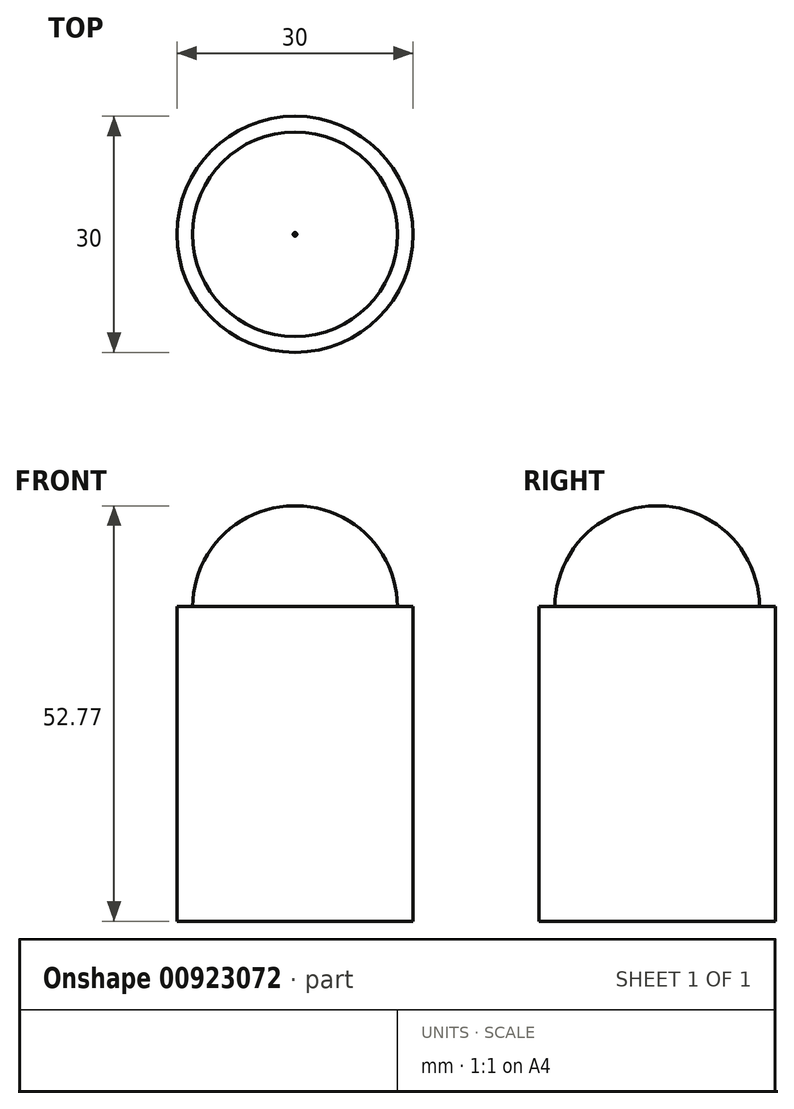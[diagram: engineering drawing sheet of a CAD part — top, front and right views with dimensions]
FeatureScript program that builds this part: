
annotation { "Feature Type Name" : "Feature", "Feature Type Description" : "" }
export const myFeature = defineFeature(function(context is Context, id is Id, definition is map)
    precondition{}
    {
        {
            var Q0;
            Q0=qCreatedBy(makeId("Top.planeOp"),FACE);
            var sketch = newSketch(context, id + "F0", { "sketchPlane" : qUnion([Q0])});
            skCircle(sketch, "E0", {"center": v(0, 0) * mm, "radius": 15 * mm});
            skSolve(sketch);
        }
        {
            var Q0;
            Q0=makeQuery(id+"F0.imprint","IMPRINT",FACE,{"disambiguationData":[TD([[makeQuery(id+"F0.imprint","IMPRINT",EDGE,{"derivedFrom":sQuery(id+"F0.wireOp",EDGE,"E0")}),1.0]])]});
            extrude(context, id + "F1", {"entities" : qUnion([Q0]), "depth" : 25 * mm, "offsetDistance" : 25 * mm});
        }
        {
            var Q0;
            Q0=qCreatedBy(makeId("Front.planeOp"),FACE);
            var sketch = newSketch(context, id + "F2", { "sketchPlane" : qUnion([Q0])});
            skLineSegment(sketch, "E1", {"start": v(-15, 25) * mm, "end": v(0, 25) * mm});
            skLineSegment(sketch, "E2", {"start": v(0, 25) * mm, "end": v(0, 27) * mm});
            skLineSegment(sketch, "E3", {"start": v(0, 27) * mm, "end": v(0, 42) * mm});
            skLineSegment(sketch, "E4", {"start": v(-15, 25) * mm, "end": v(-15, 40) * mm});
            skLineSegment(sketch, "E5", {"start": v(-15, 40) * mm, "end": v(-13, 40) * mm});
            skArc(sketch, "E6", {"start": v(-13, 40) * mm, "mid": v(-9.23, 30.77) * mm, "end": v(0, 27) * mm});
            skSolve(sketch);
        }
        {
            var Q0;
            Q0=makeQuery(id+"F2.imprint","IMPRINT",FACE,{"disambiguationData":[TD([[makeQuery(id+"F2.imprint","IMPRINT",EDGE,{"derivedFrom":sQuery(id+"F2.wireOp",EDGE,"E1")}),1.0]])]});
            var Q1;
            Q1=sQuery(id+"F2.wireOp",EDGE,"E2");
            revolve(context, id + "F3", {"operationType" : NewBodyOperationType.ADD, "surfaceOperationType" : NewSurfaceOperationType.NEW, "entities" : qUnion([Q0]), "axis" : qUnion([Q1]), "revolveType" : RevolveType.FULL});
        }
    });
